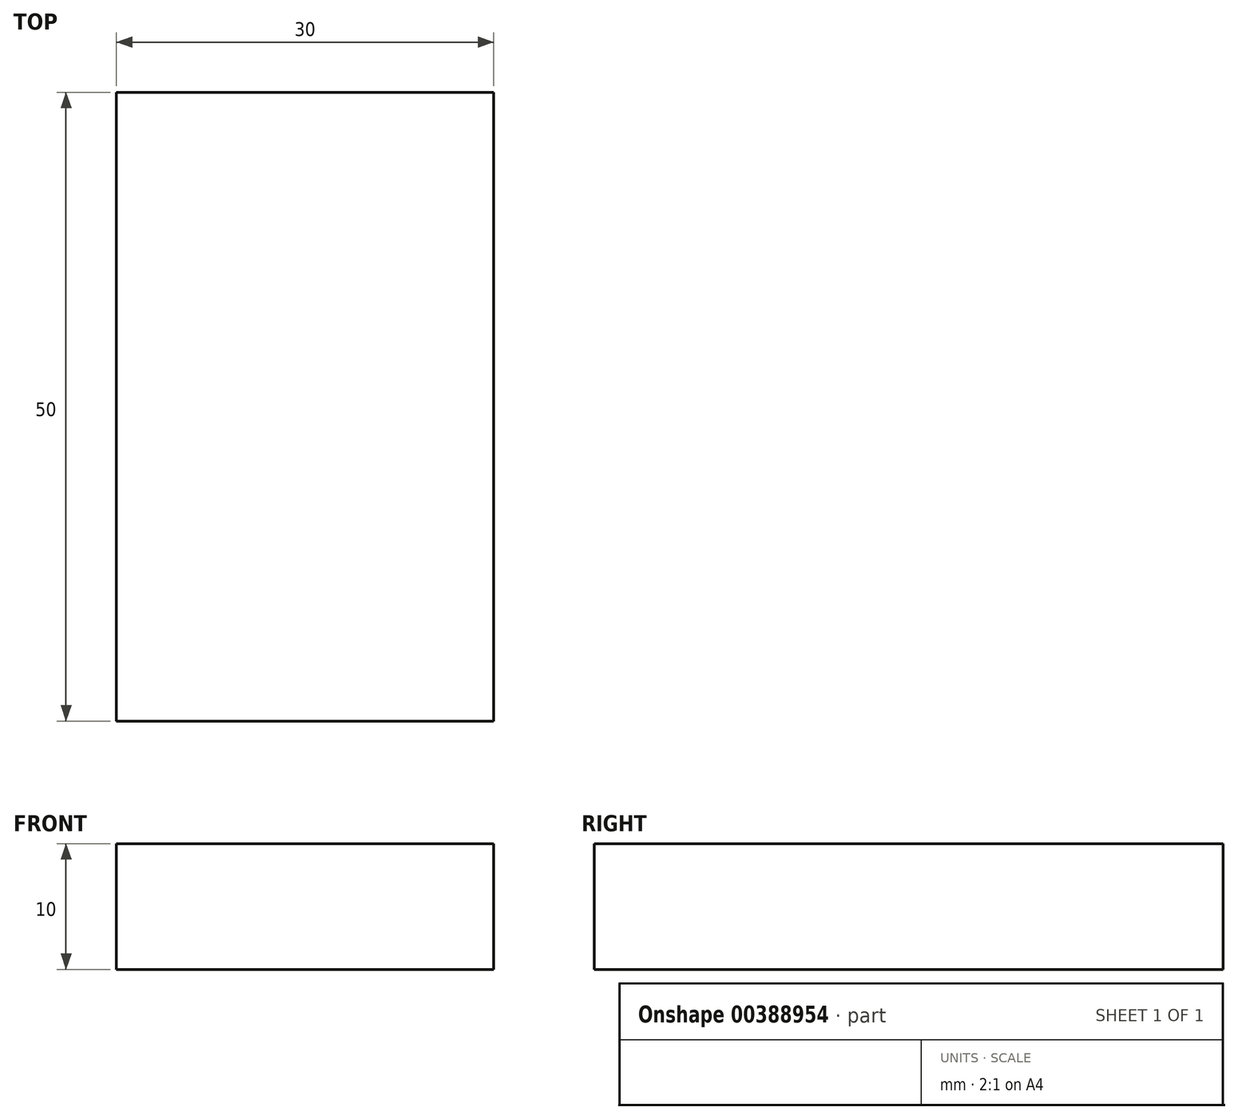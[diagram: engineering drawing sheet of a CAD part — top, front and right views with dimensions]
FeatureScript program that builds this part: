
annotation { "Feature Type Name" : "Feature", "Feature Type Description" : "" }
export const myFeature = defineFeature(function(context is Context, id is Id, definition is map)
    precondition{}
    {
        {
            var Q0;
            Q0=qCreatedBy(makeId("Top.planeOp"),FACE);
            var sketch = newSketch(context, id + "F0", { "sketchPlane" : qUnion([Q0])});
            skLineSegment(sketch, "E0.bottom", {"start": v(0, 0) * mm, "end": v(30, 0) * mm});
            skLineSegment(sketch, "E0.top", {"start": v(0, 50) * mm, "end": v(30, 50) * mm});
            skLineSegment(sketch, "E0.left", {"start": v(0, 0) * mm, "end": v(0, 50) * mm});
            skLineSegment(sketch, "E0.right", {"start": v(30, 0) * mm, "end": v(30, 50) * mm});
            skSolve(sketch);
        }
        {
            var Q0;
            Q0 = qSketchRegion(id + "F0", true);
            extrude(context, id + "F1", {"entities" : qUnion([Q0]), "depth" : 10 * mm});
        }
    });
